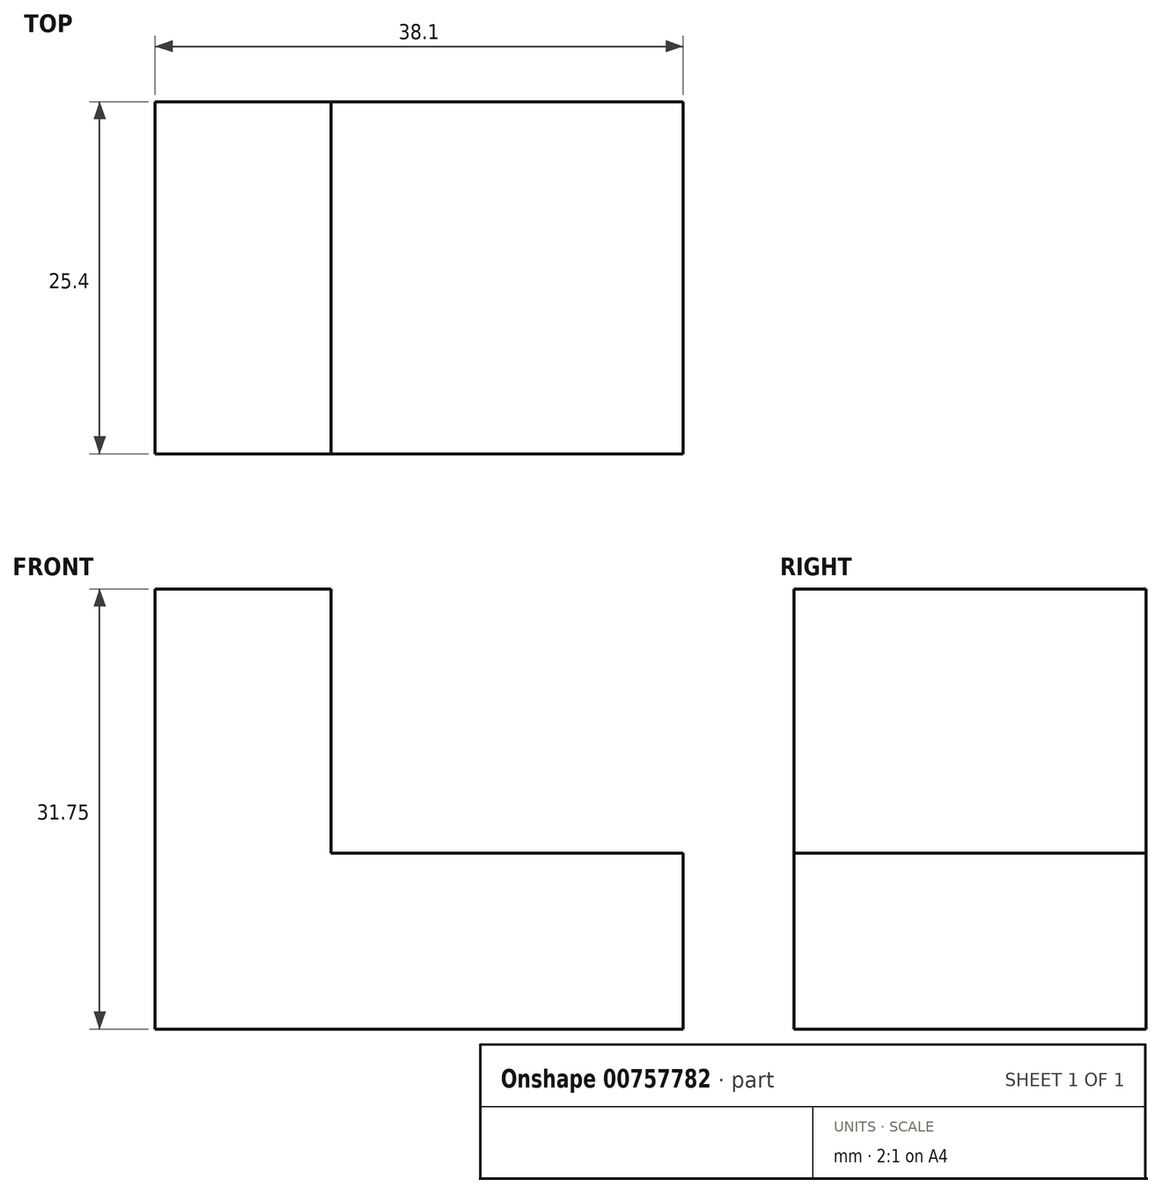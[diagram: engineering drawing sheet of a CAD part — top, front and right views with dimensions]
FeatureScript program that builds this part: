
annotation { "Feature Type Name" : "Feature", "Feature Type Description" : "" }
export const myFeature = defineFeature(function(context is Context, id is Id, definition is map)
    precondition{}
    {
        {
            var Q0;
            Q0=qCreatedBy(makeId("Front.planeOp"),FACE);
            var sketch = newSketch(context, id + "F0", { "sketchPlane" : qUnion([Q0])});
            skLineSegment(sketch, "E0", {"start": v(19.73, 0) * mm, "end": v(-18.37, 0) * mm});
            skLineSegment(sketch, "E1", {"start": v(-18.37, 0) * mm, "end": v(-18.37, 31.75) * mm});
            skLineSegment(sketch, "E2", {"start": v(-18.37, 31.75) * mm, "end": v(-5.67, 31.75) * mm});
            skLineSegment(sketch, "E3", {"start": v(-5.67, 31.75) * mm, "end": v(-5.67, 12.7) * mm});
            skLineSegment(sketch, "E4", {"start": v(-5.67, 12.7) * mm, "end": v(19.73, 12.7) * mm});
            skLineSegment(sketch, "E5", {"start": v(19.73, 12.7) * mm, "end": v(19.73, 0) * mm});
            skSolve(sketch);
        }
        {
            var Q0;
            Q0 = qSketchRegion(id + "F0", true);
            extrude(context, id + "F1", {"entities" : qUnion([Q0]), "depth" : 25.4 * mm, "offsetDistance" : 25.4 * mm});
        }
    });
